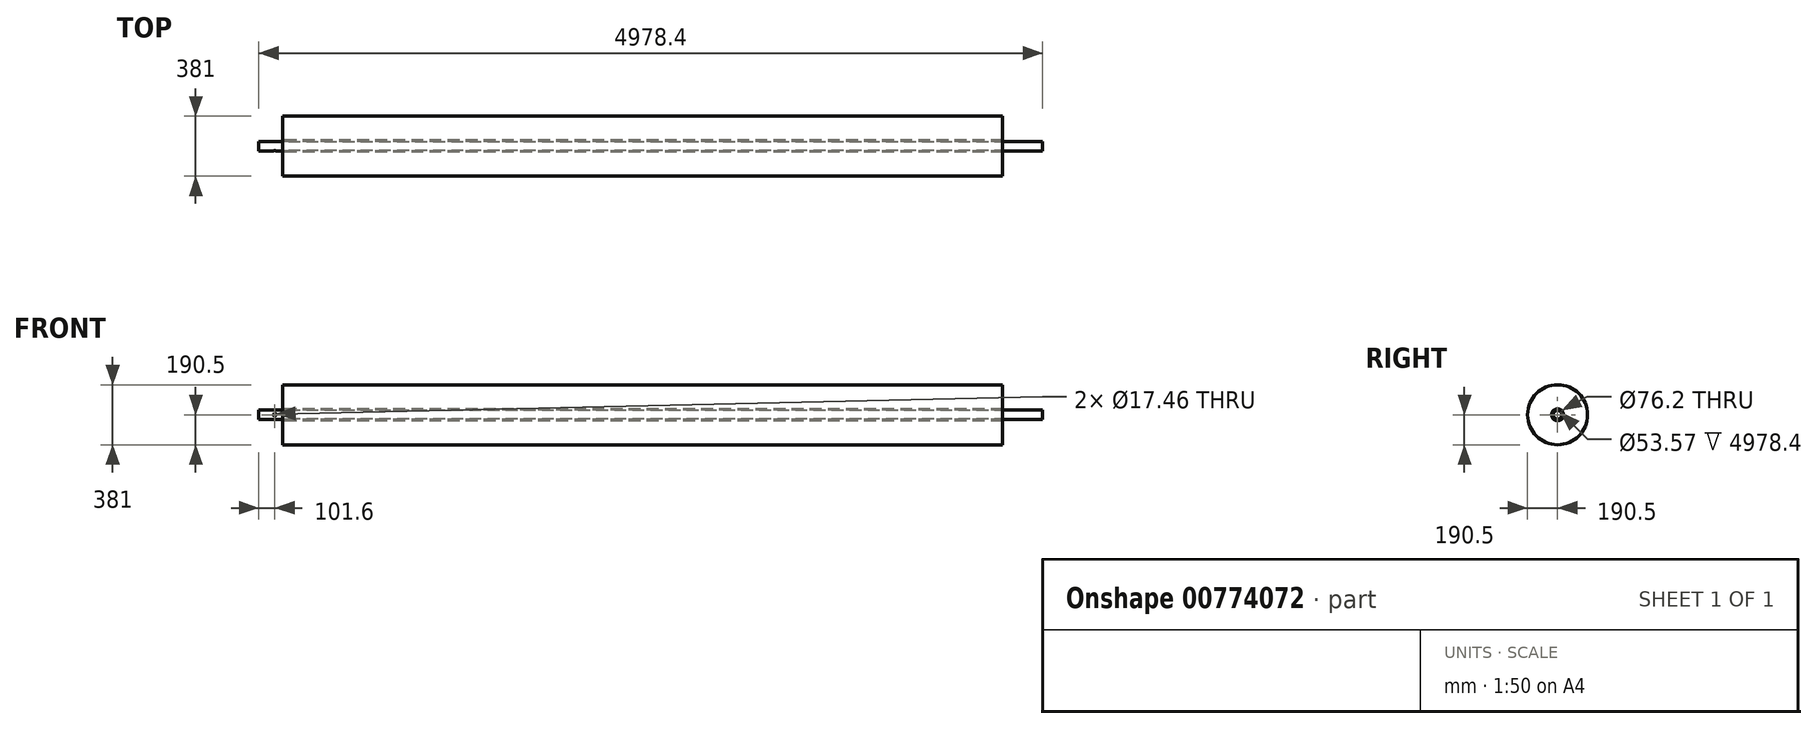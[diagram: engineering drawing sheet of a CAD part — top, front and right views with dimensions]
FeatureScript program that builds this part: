
annotation { "Feature Type Name" : "Feature", "Feature Type Description" : "" }
export const myFeature = defineFeature(function(context is Context, id is Id, definition is map)
    precondition{}
    {
        {
            var Q0;
            Q0=qCreatedBy(makeId("Front.planeOp"),FACE);
            var sketch = newSketch(context, id + "F0", { "sketchPlane" : qUnion([Q0])});
            skLineSegment(sketch, "E0", {"start": v(-2286, 0) * mm, "end": v(2286, 0) * mm, "construction": true});
            skLineSegment(sketch, "E1", {"start": v(2286, 38.1) * mm, "end": v(2286, 190.5) * mm});
            skLineSegment(sketch, "E2", {"start": v(-2286, 190.5) * mm, "end": v(2286, 190.5) * mm});
            skLineSegment(sketch, "E3", {"start": v(-2286, 190.5) * mm, "end": v(-2286, 38.1) * mm});
            skLineSegment(sketch, "E4", {"start": v(2286, 38.1) * mm, "end": v(-2286, 38.1) * mm});
            skLineSegment(sketch, "E5", {"start": v(2540, 30.16) * mm, "end": v(2540, 26.78) * mm});
            skLineSegment(sketch, "E6", {"start": v(2540, 26.78) * mm, "end": v(-2438.4, 26.78) * mm});
            skLineSegment(sketch, "E7", {"start": v(-2438.4, 26.78) * mm, "end": v(-2438.4, 30.16) * mm});
            skLineSegment(sketch, "E8", {"start": v(-2438.4, 30.16) * mm, "end": v(2540, 30.16) * mm});
            skSolve(sketch);
        }
        {
            var Q0;
            Q0 = qSketchRegion(id + "F0", true);
            var Q1;
            Q1=sQuery(id+"F0.wireOp",EDGE,"E0");
            revolve(context, id + "F1", {"surfaceOperationType" : NewSurfaceOperationType.NEW, "entities" : qUnion([Q0]), "axis" : qUnion([Q1]), "revolveType" : RevolveType.FULL});
        }
        {
            var Q0;
            Q0=qCreatedBy(makeId("Front.planeOp"),FACE);
            var sketch = newSketch(context, id + "F2", { "sketchPlane" : qUnion([Q0])});
            skCircle(sketch, "E9", {"center": v(-2336.8, 0) * mm, "radius": 8.73 * mm});
            skSolve(sketch);
        }
        {
            var Q0;
            Q0 = qSketchRegion(id + "F2", true);
            extrude(context, id + "F3", {"entities" : qUnion([Q0]), "operationType" : NewBodyOperationType.REMOVE, "endBound" : BoundingType.THROUGH_ALL, "oppositeDirection" : true, "depth" : 25.4 * mm, "offsetDistance" : 25.4 * mm, "hasSecondDirection" : true, "secondDirectionBound" : SecondDirectionBoundingType.THROUGH_ALL, "secondDirectionOppositeDirection" : false, "secondDirectionDepth" : 25.4 * mm});
        }
    });
